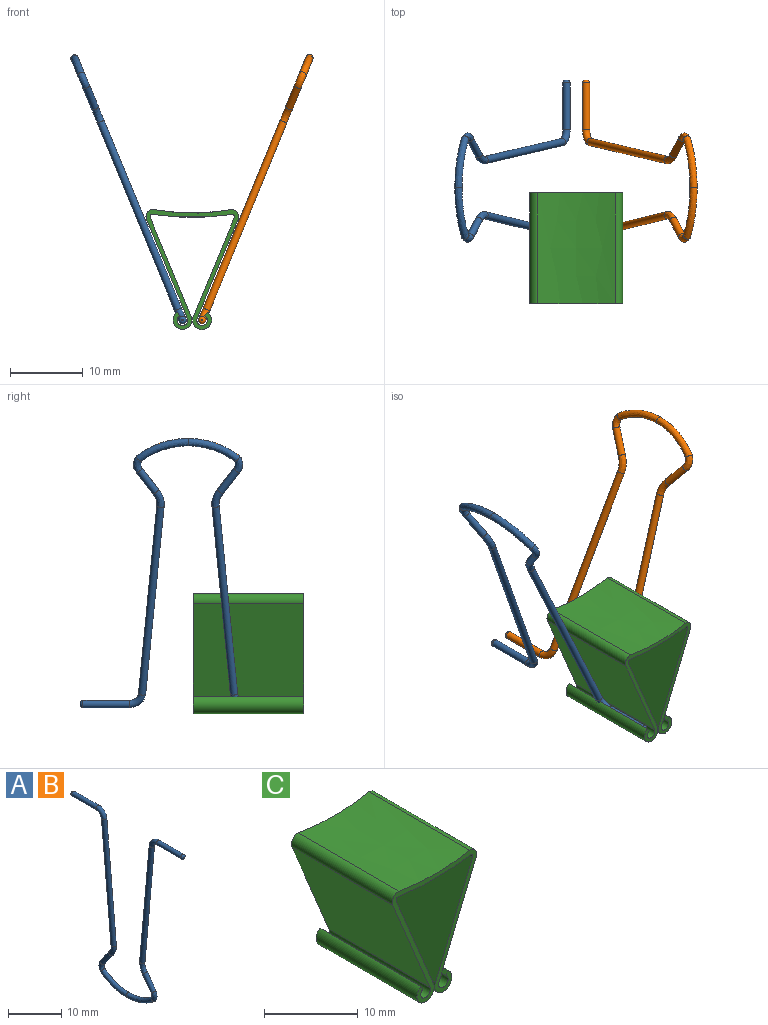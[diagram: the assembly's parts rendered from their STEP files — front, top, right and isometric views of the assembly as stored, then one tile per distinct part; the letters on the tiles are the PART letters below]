
ASSEMBLY  parts=3 mates=2
PART A: 18 faces, bbox 2x29.7x40.1 mm
  f0: plane 0.2x0.2mm, normal (0,1,0), area 0mm2, adj f16
  f1: plane 0.2x0.2mm, normal (0,-1,0), area 0mm2, adj f17
  f2: cylinder r=0.5mm len=27.98mm, axis (0,0.09,1), area 88mm2, adj f3,f5
  f3: torus R=1.71mm, axis (-1,0,0), area 7.9mm2, adj f2,f4
  f4: cylinder r=0.5mm len=6.42mm, axis (0,1,0), area 20.2mm2, adj f3,f16
  f5: bspline ~2.55x1.59mm, area 7.3mm2, adj f2,f7
  f6: bspline ~2.45x2mm, area 5.8mm2, adj f7,f9
  f7: cylinder r=0.5mm len=3.76mm, axis (0,-0.58,0.81), area 12.2mm2, adj f5,f6
  f8: bspline ~7.21x3.45mm, area 23mm2, adj f9,f10
  f9: bspline ~7.21x3.45mm, area 23mm2, adj f6,f8
  f10: bspline ~2.45x2mm, area 5.8mm2, adj f8,f11
  f11: cylinder r=0.5mm len=3.76mm, axis (0,-0.58,-0.81), area 12.2mm2, adj f10,f15
  f12: cylinder r=0.5mm len=6.42mm, axis (0,1,0), area 20.2mm2, adj f13,f17
  f13: torus R=1.71mm, axis (-1,0,0), area 7.9mm2, adj f12,f14
  f14: cylinder r=0.5mm len=27.98mm, axis (0,0.09,-1), area 88mm2, adj f13,f15
  f15: bspline ~2.55x1.59mm, area 7.3mm2, adj f11,f14
  f16: torus R=0.1mm, axis (0,-1,0), area 1.4mm2, adj f0,f4
  f17: torus R=0.1mm, axis (0,-1,0), area 1.4mm2, adj f1,f12
PART B: same geometry as A
PART C: 18 faces, bbox 12.7x15.2x16.5 mm
  f0: cylinder r=1mm len=15.24mm, axis (0,1,0), area 30.1mm2, adj f1,f15,f16,f17
  f1: extruded ~15.24x10.71mm, area 164.1mm2, adj f0,f2,f16,f17
  f2: cylinder r=1mm len=15.24mm, axis (0,1,0), area 30.1mm2, adj f1,f3,f16,f17
  f3: plane 15.24x13.54mm, normal (-0.92,0,-0.38), area 223.3mm2, adj f2,f4,f16,f17
  f4: cylinder r=0.72mm len=15.24mm, axis (0,1,0), area 49.9mm2, adj f3,f5,f16,f17
  f5: plane 15.24x0.48mm, normal (0.84,0,0.54), area 8.8mm2, adj f4,f6,f16,f17
  f6: cylinder r=1.3mm len=15.24mm, axis (0,1,0), area 89.5mm2, adj f5,f7,f16,f17
  f7: plane 15.24x13.54mm, normal (0.92,0,0.38), area 223.3mm2, adj f6,f8,f16,f17
  f8: cylinder r=0.43mm len=15.24mm, axis (0,1,0), area 8.4mm2, adj f7,f9,f16,f17
  f9: extruded ~15.24x11.25mm, area 172.1mm2, adj f8,f10,f16,f17
  f10: cylinder r=0.43mm len=15.24mm, axis (0,1,0), area 8.4mm2, adj f9,f11,f16,f17
  f11: plane 15.24x13.54mm, normal (-0.92,0,0.38), area 223.3mm2, adj f10,f12,f16,f17
  f12: cylinder r=1.3mm len=15.24mm, axis (0,1,0), area 89.5mm2, adj f11,f13,f16,f17
  f13: plane 15.24x0.48mm, normal (-0.84,0,0.54), area 8.8mm2, adj f12,f14,f16,f17
  f14: cylinder r=0.72mm len=15.24mm, axis (0,1,0), area 49.9mm2, adj f13,f15,f16,f17
  f15: plane 15.24x13.54mm, normal (0.92,0,-0.38), area 223.3mm2, adj f0,f14,f16,f17
  f16: plane 16.49x12.73mm, normal (0,-1,0), area 30.4mm2, adj f0,f1,f2,f3,f4,f5,f6,f7
  f17: plane 16.49x12.73mm, normal (0,1,0), area 30.4mm2, adj f0,f1,f2,f3,f4,f5,f6,f7
PLACE A rot(axis=(0,1,0),157.6deg) t=(-1.32,16.62,0.26)mm
PLACE B rot(axis=(0,-1,0),157.7deg) t=(1.38,16.62,0.26)mm
PLACE C t=(0.03,15.94,0.54)mm fixed
MATE revolute A.f4 <-> C.f4  axis (0,1,0) through (-1.32,5.4,0.26)mm
MATE revolute B.f4 <-> C.f12  axis (0,1,0) through (1.38,5.4,0.26)mm
